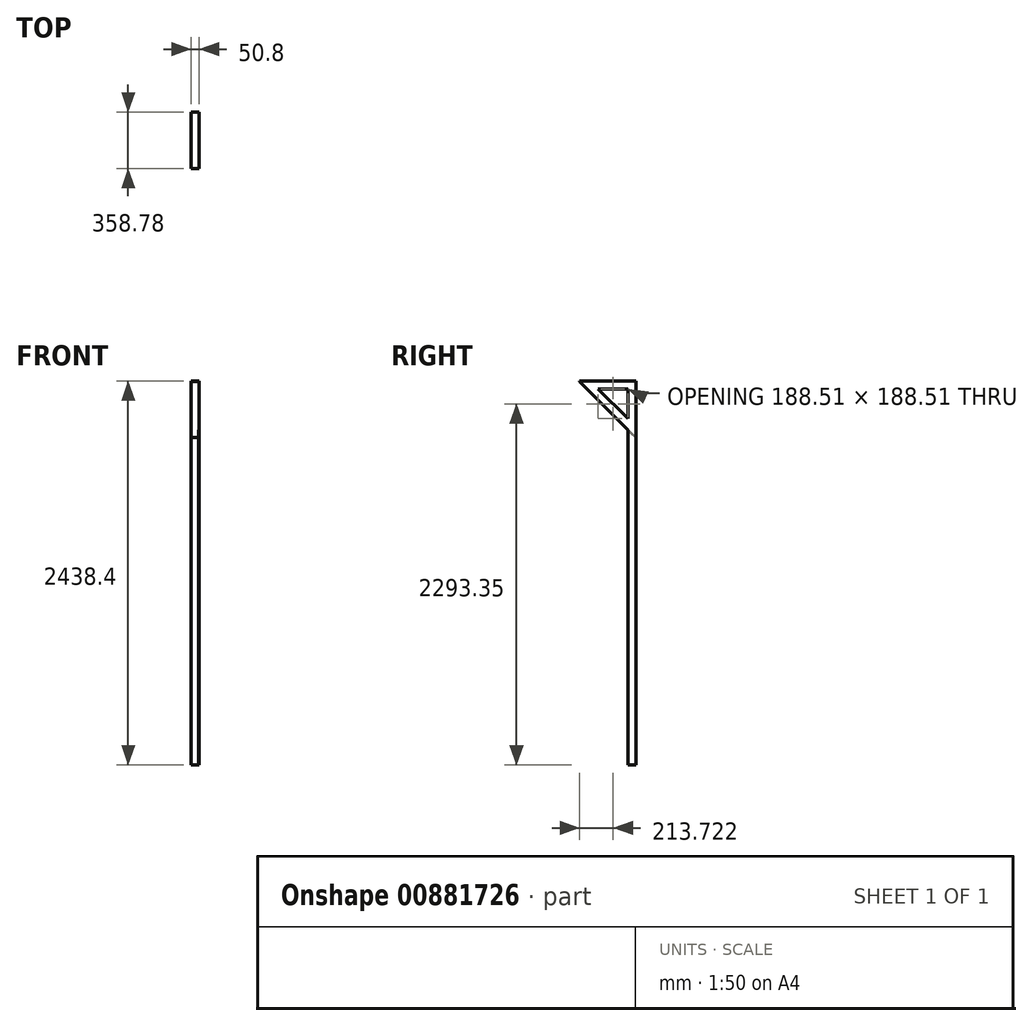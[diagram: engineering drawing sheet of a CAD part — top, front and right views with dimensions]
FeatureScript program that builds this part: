
annotation { "Feature Type Name" : "Feature", "Feature Type Description" : "" }
export const myFeature = defineFeature(function(context is Context, id is Id, definition is map)
    precondition{}
    {
        {
            var Q0;
            Q0=qCreatedBy(makeId("Top.planeOp"),FACE);
            var sketch = newSketch(context, id + "F0", { "sketchPlane" : qUnion([Q0])});
            skLineSegment(sketch, "E0", {"start": v(-13.15, 22.92) * mm, "end": v(37.65, 22.92) * mm});
            skLineSegment(sketch, "E1", {"start": v(37.65, 22.92) * mm, "end": v(37.65, -27.88) * mm});
            skLineSegment(sketch, "E2", {"start": v(37.65, -27.88) * mm, "end": v(34.47, -27.88) * mm});
            skLineSegment(sketch, "E3", {"start": v(34.47, -27.88) * mm, "end": v(34.47, 19.74) * mm});
            skLineSegment(sketch, "E4", {"start": v(34.47, 19.74) * mm, "end": v(-13.15, 19.74) * mm});
            skLineSegment(sketch, "E5", {"start": v(-13.15, 19.74) * mm, "end": v(-13.15, 22.92) * mm});
            skSolve(sketch);
        }
        {
            var Q0;
            Q0=makeQuery(id+"F0.imprint","IMPRINT",FACE,{"disambiguationData":[TD([[makeQuery(id+"F0.imprint","IMPRINT",EDGE,{"derivedFrom":sQuery(id+"F0.wireOp",EDGE,"E0")}),-1.0]])]});
            extrude(context, id + "F1", {"entities" : qUnion([Q0]), "depth" : 2438.4 * mm, "offsetDistance" : 25.4 * mm});
        }
        {
            var Q0;
            Q0=makeQuery(id+"F1.opExtrude","SWEPT_FACE",FACE,{"disambiguationData":[OSD([sQuery(id+"F0.wireOp",EDGE,"E2")])]});
            var sketch = newSketch(context, id + "F2", { "sketchPlane" : qUnion([Q0])});
            skLineSegment(sketch, "E6", {"start": v(34.47, 2438.4) * mm, "end": v(37.65, 2438.4) * mm});
            skLineSegment(sketch, "E7", {"start": v(37.65, 2438.4) * mm, "end": v(37.65, 2387.6) * mm});
            skLineSegment(sketch, "E8", {"start": v(37.65, 2387.6) * mm, "end": v(34.47, 2387.6) * mm});
            skLineSegment(sketch, "E9", {"start": v(34.47, 2387.6) * mm, "end": v(34.47, 2438.4) * mm});
            skSolve(sketch);
        }
        {
            var Q0;
            Q0 = qSketchRegion(id + "F2", true);
            extrude(context, id + "F3", {"entities" : qUnion([Q0]), "operationType" : NewBodyOperationType.REMOVE, "oppositeDirection" : true, "depth" : 47.62 * mm, "offsetDistance" : 25.4 * mm});
        }
        {
            var Q0;
            Q0=makeQuery(id+"F3.boolean.opBoolean","MERGE",FACE,{"derivedFrom":[makeQuery(id+"F1.opExtrude","SWEPT_FACE",FACE,{"disambiguationData":[OSD([sQuery(id+"F0.wireOp",EDGE,"E4")])]})],"fromTools":[makeQuery(id+"F3.opExtrude","CAP_FACE",FACE,{"disambiguationData":[OSD([sQuery(id+"F2.wireOp",EDGE,"E6"),sQuery(id+"F2.wireOp",EDGE,"E7"),sQuery(id+"F2.wireOp",EDGE,"E8"),sQuery(id+"F2.wireOp",EDGE,"E9")])],"isStart":false})]});
            var sketch = newSketch(context, id + "F4", { "sketchPlane" : qUnion([Q0])});
            skLineSegment(sketch, "E10", {"start": v(-13.15, 2438.4) * mm, "end": v(37.65, 2438.4) * mm});
            skLineSegment(sketch, "E11", {"start": v(37.65, 2438.4) * mm, "end": v(37.65, 2387.6) * mm});
            skLineSegment(sketch, "E12", {"start": v(37.65, 2387.6) * mm, "end": v(34.47, 2387.6) * mm});
            skLineSegment(sketch, "E13", {"start": v(34.47, 2387.6) * mm, "end": v(34.47, 2435.22) * mm});
            skLineSegment(sketch, "E14", {"start": v(34.47, 2435.22) * mm, "end": v(-13.15, 2435.22) * mm});
            skLineSegment(sketch, "E15", {"start": v(-13.15, 2435.22) * mm, "end": v(-13.15, 2438.4) * mm});
            skSolve(sketch);
        }
        {
            var Q0;
            Q0 = qSketchRegion(id + "F4", true);
            extrude(context, id + "F5", {"entities" : qUnion([Q0]), "operationType" : NewBodyOperationType.ADD, "depth" : 355.6 * mm, "offsetDistance" : 25.4 * mm});
        }
        {
            var Q0;
            Q0=makeQuery(id+"F5.boolean.opBoolean","MERGE",FACE,{"derivedFrom":[makeQuery(id+"F1.opExtrude","SWEPT_FACE",FACE,{"disambiguationData":[OSD([sQuery(id+"F0.wireOp",EDGE,"E3")])]}),makeQuery(id+"F5.opExtrude","SWEPT_FACE",FACE,{"disambiguationData":[OSD([sQuery(id+"F4.wireOp",EDGE,"E13")])]})]});
            var sketch = newSketch(context, id + "F6", { "sketchPlane" : qUnion([Q0])});
            skLineSegment(sketch, "E16", {"start": v(335.86, 2435.22) * mm, "end": v(-19.74, 2079.62) * mm});
            skLineSegment(sketch, "E17", {"start": v(-19.74, 2079.62) * mm, "end": v(-19.74, 2084.12) * mm});
            skLineSegment(sketch, "E18", {"start": v(-19.74, 2084.12) * mm, "end": v(331.37, 2435.22) * mm});
            skLineSegment(sketch, "E19", {"start": v(331.37, 2435.22) * mm, "end": v(335.86, 2435.22) * mm});
            skSolve(sketch);
        }
        {
            var Q0;
            Q0 = qSketchRegion(id + "F6", true);
            extrude(context, id + "F7", {"entities" : qUnion([Q0]), "operationType" : NewBodyOperationType.ADD, "depth" : 47.62 * mm, "offsetDistance" : 25.4 * mm});
        }
        {
            var Q0;
            Q0=makeQuery(id+"F7.opExtrude","CAP_FACE",FACE,{"disambiguationData":[OSD([sQuery(id+"F6.wireOp",EDGE,"E16"),sQuery(id+"F6.wireOp",EDGE,"E17"),sQuery(id+"F6.wireOp",EDGE,"E18"),sQuery(id+"F6.wireOp",EDGE,"E19")])],"isStart":true});
            var sketch = newSketch(context, id + "F8", { "sketchPlane" : qUnion([Q0])});
            skLineSegment(sketch, "E20", {"start": v(-288.23, 2387.6) * mm, "end": v(-27.88, 2127.25) * mm});
            skLineSegment(sketch, "E21", {"start": v(-27.88, 2127.25) * mm, "end": v(-27.88, 2199.1) * mm});
            skLineSegment(sketch, "E22", {"start": v(-27.88, 2199.1) * mm, "end": v(-216.4, 2387.6) * mm});
            skLineSegment(sketch, "E23", {"start": v(-216.4, 2387.6) * mm, "end": v(-288.23, 2387.6) * mm});
            skSolve(sketch);
        }
        {
            var Q0;
            Q0 = qSketchRegion(id + "F8", true);
            extrude(context, id + "F9", {"entities" : qUnion([Q0]), "operationType" : NewBodyOperationType.ADD, "depth" : 3.17 * mm, "offsetDistance" : 25.4 * mm});
        }
        {
            var Q0;
            {var subQ0=sQuery(id+"F4.wireOp",EDGE,"E13");var subQ1=sQuery(id+"F4.wireOp",EDGE,"E12");Q0=makeQuery(id+"F7.boolean.opBoolean","SPLIT",FACE,{"disambiguationData":[TD([makeQuery(id+"F5.opExtrude","CAP_FACE",FACE,{"disambiguationData":[OSD([sQuery(id+"F4.wireOp",EDGE,"E10"),sQuery(id+"F4.wireOp",EDGE,"E11"),subQ1,subQ0,sQuery(id+"F4.wireOp",EDGE,"E14"),sQuery(id+"F4.wireOp",EDGE,"E15")])],"isStart":false})])],"derivedFrom":makeQuery(id+"F5.boolean.opBoolean","MERGE",FACE,{"derivedFrom":[makeQuery(id+"F1.opExtrude","SWEPT_FACE",FACE,{"disambiguationData":[OSD([sQuery(id+"F0.wireOp",EDGE,"E3")])]}),makeQuery(id+"F5.opExtrude","SWEPT_FACE",FACE,{"disambiguationData":[OSD([subQ0])]})]})});}
            var sketch = newSketch(context, id + "F10", { "sketchPlane" : qUnion([Q0])});
            skLineSegment(sketch, "E24", {"start": v(335.86, 2435.22) * mm, "end": v(335.86, 2387.6) * mm});
            skLineSegment(sketch, "E25", {"start": v(335.86, 2387.6) * mm, "end": v(288.23, 2387.6) * mm});
            skLineSegment(sketch, "E26", {"start": v(288.23, 2387.6) * mm, "end": v(335.86, 2435.22) * mm});
            skSolve(sketch);
        }
        {
            var Q0;
            Q0 = qSketchRegion(id + "F10", true);
            extrude(context, id + "F11", {"entities" : qUnion([Q0]), "operationType" : NewBodyOperationType.REMOVE, "oppositeDirection" : true, "depth" : 25.4 * mm, "offsetDistance" : 25.4 * mm});
        }
    });
